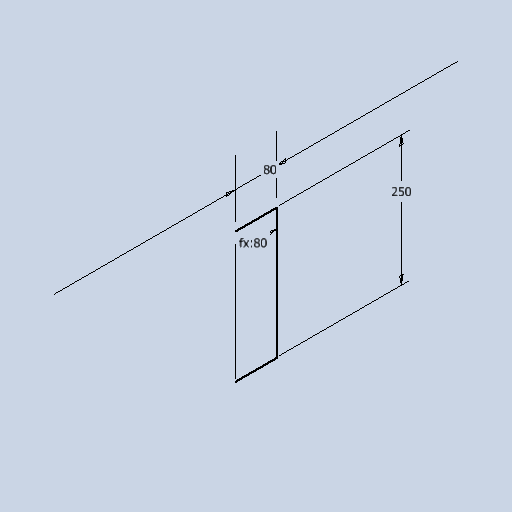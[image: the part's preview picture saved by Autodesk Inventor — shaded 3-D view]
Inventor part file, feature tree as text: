
AUTODESK INVENTOR PART (.ipt)
format: ipt  version: 2024.3 (Build 283343000, 343)  size: 233,472 bytes
history: native  units: mm
features: sketch x1
ambient origin geometry x8: Origin, YZ Plane, XZ Plane, XY Plane, X Axis, Y Axis, Z Axis, Center Point
feature tree (1):
  sketch  "Sketch1"  dims[d3=80.0mm d4=80.0mm d5=250.0mm]
